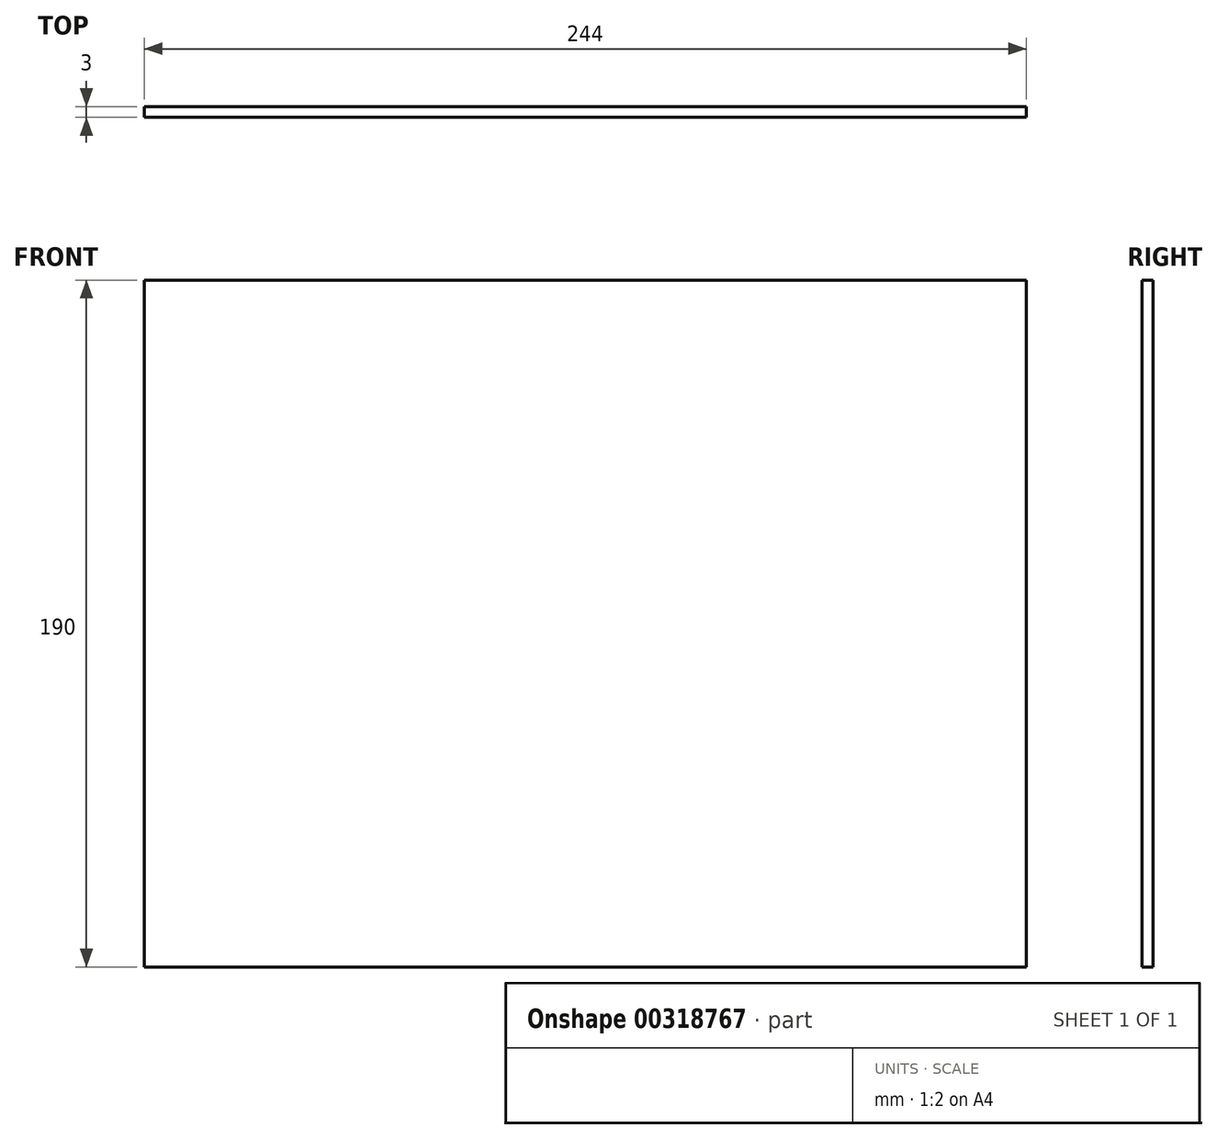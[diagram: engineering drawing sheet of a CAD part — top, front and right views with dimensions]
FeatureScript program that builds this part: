
annotation { "Feature Type Name" : "Feature", "Feature Type Description" : "" }
export const myFeature = defineFeature(function(context is Context, id is Id, definition is map)
    precondition{}
    {
        {
            var Q0;
            Q0=qCreatedBy(makeId("Front.planeOp"),FACE);
            var sketch = newSketch(context, id + "F0", { "sketchPlane" : qUnion([Q0])});
            skLineSegment(sketch, "E0.bottom", {"start": v(122, -95) * mm, "end": v(-122, -95) * mm});
            skLineSegment(sketch, "E0.top", {"start": v(122, 95) * mm, "end": v(-122, 95) * mm});
            skLineSegment(sketch, "E0.left", {"start": v(122, -95) * mm, "end": v(122, 95) * mm});
            skLineSegment(sketch, "E0.right", {"start": v(-122, -95) * mm, "end": v(-122, 95) * mm});
            skPoint(sketch, "E0.middle", {"position": v(0, 0) * mm});
            skSolve(sketch);
        }
        {
            var Q0;
            Q0=makeQuery(id+"F0.imprint","IMPRINT",FACE,{"disambiguationData":[TD([[makeQuery(id+"F0.imprint","IMPRINT",EDGE,{"derivedFrom":sQuery(id+"F0.wireOp",EDGE,"E0.bottom")}),-1.0]])]});
            extrude(context, id + "F1", {"entities" : qUnion([Q0]), "depth" : 3 * mm, "offsetDistance" : 25 * mm});
        }
    });
